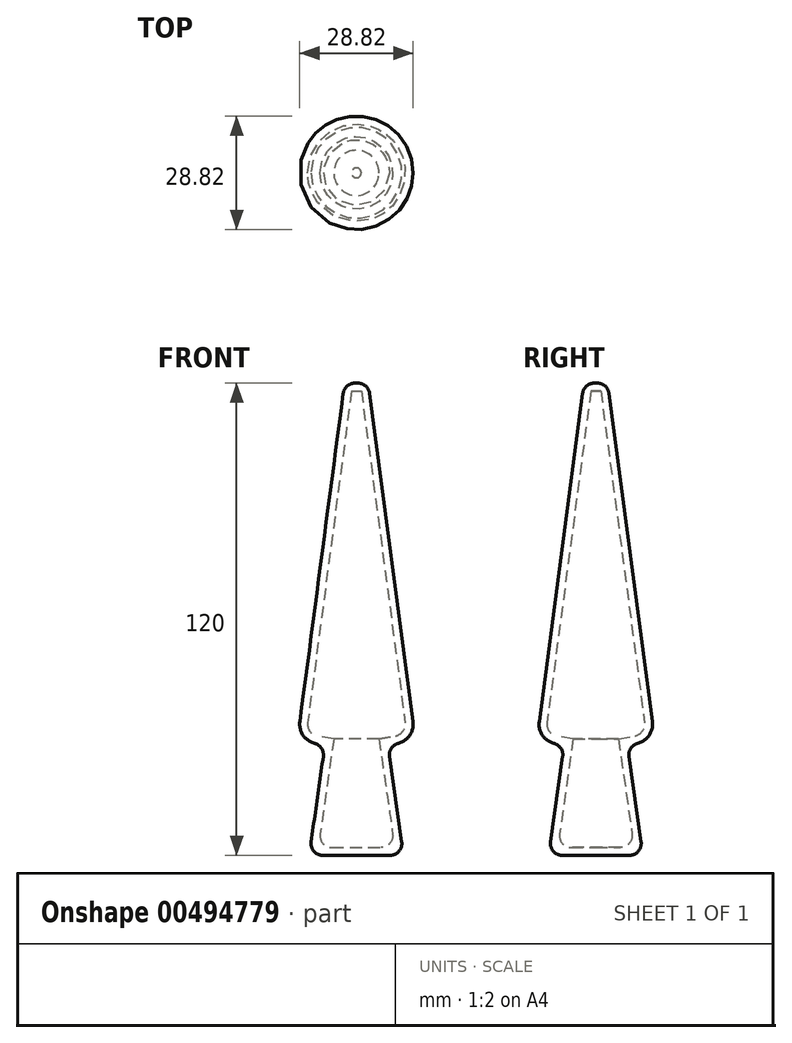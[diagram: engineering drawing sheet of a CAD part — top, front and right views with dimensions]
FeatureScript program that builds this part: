
annotation { "Feature Type Name" : "Feature", "Feature Type Description" : "" }
export const myFeature = defineFeature(function(context is Context, id is Id, definition is map)
    precondition{}
    {
        {
            var Q0;
            Q0=qCreatedBy(makeId("Front.planeOp"),FACE);
            var sketch = newSketch(context, id + "F0", { "sketchPlane" : qUnion([Q0])});
            skLineSegment(sketch, "E0", {"start": v(8, 8) * mm, "end": v(15, 9.22) * mm});
            skLineSegment(sketch, "E1", {"start": v(15, 9.22) * mm, "end": v(3, 100) * mm});
            skLineSegment(sketch, "E2", {"start": v(0, 100) * mm, "end": v(0, -20) * mm});
            skLineSegment(sketch, "E3", {"start": v(0, -27) * mm, "end": v(0, -53.61) * mm});
            skLineSegment(sketch, "E4", {"start": v(0, 100) * mm, "end": v(3, 100) * mm});
            skLineSegment(sketch, "E5", {"start": v(0, 103.57) * mm, "end": v(0, 117.09) * mm});
            skLineSegment(sketch, "E6", {"start": v(0, -20) * mm, "end": v(12, -20) * mm});
            skLineSegment(sketch, "E7", {"start": v(8, 8) * mm, "end": v(12, -20) * mm});
            skSolve(sketch);
        }
        {
            var Q0;
            Q0=makeQuery(id+"F0.imprint","IMPRINT",FACE,{"disambiguationData":[TD([[makeQuery(id+"F0.imprint","IMPRINT",EDGE,{"derivedFrom":sQuery(id+"F0.wireOp",EDGE,"E0")}),1.0]])]});
            var Q1;
            Q1=sQuery(id+"F0.wireOp",EDGE,"E5");
            revolve(context, id + "F1", {"entities" : qUnion([Q0]), "axis" : qUnion([Q1]), "revolveType" : RevolveType.ONE_DIRECTION, "angle" : 180 * degree});
        }
        {
            var Q0;
            Q0=makeQuery(id+"F1.opRevolve","CAP_FACE",FACE,{"disambiguationData":[OSD([sQuery(id+"F0.wireOp",EDGE,"E0"),sQuery(id+"F0.wireOp",EDGE,"E1"),sQuery(id+"F0.wireOp",EDGE,"E2"),sQuery(id+"F0.wireOp",EDGE,"E4"),sQuery(id+"F0.wireOp",EDGE,"E6"),sQuery(id+"F0.wireOp",EDGE,"E7")])],"isStart":false});
            shell(context, id + "F2", {"entities" : qUnion([Q0]), "thickness" : 2 * mm});
        }
        {
            var Q0;
            Q0=makeQuery(id+"F1.opRevolve","SWEPT_BODY",BODY,{"disambiguationData":[OSD([sQuery(id+"F0.wireOp",EDGE,"E0"),sQuery(id+"F0.wireOp",EDGE,"E1"),sQuery(id+"F0.wireOp",EDGE,"E2"),sQuery(id+"F0.wireOp",EDGE,"E4"),sQuery(id+"F0.wireOp",EDGE,"E6"),sQuery(id+"F0.wireOp",EDGE,"E7")])]});
            var Q1;
            Q1=qCreatedBy(makeId("Front.planeOp"),FACE);
            mirror(context, id + "F3", {"operationType" : NewBodyOperationType.ADD, "entities" : qUnion([Q0]), "mirrorPlane" : qUnion([Q1])});
        }
        {
            var Q0;
            {var subQ0=makeQuery(id+"F1.opRevolve","SWEPT_EDGE",EDGE,{"disambiguationData":[OSD([sQuery(id+"F0.wireOp",EDGE,"E0"),sQuery(id+"F0.wireOp",EDGE,"E1")])]});Q0=makeQuery(id+"F3.boolean.opBoolean","MERGE",EDGE,{"derivedFrom":[subQ0,makeQuery(id+"F3.opPattern","COPY",EDGE,{"derivedFrom":subQ0,"instanceName":"1"})]});}
            fillet(context, id + "F4", {"entities" : qUnion([Q0]), "radius" : 5 * mm, "tangentPropagation" : true, "allowEdgeOverflow" : false});
        }
        {
            var Q0;
            {var subQ0=makeQuery(id+"F1.opRevolve","SWEPT_EDGE",EDGE,{"disambiguationData":[OSD([sQuery(id+"F0.wireOp",EDGE,"E6"),sQuery(id+"F0.wireOp",EDGE,"E7")])]});Q0=makeQuery(id+"F3.boolean.opBoolean","MERGE",EDGE,{"derivedFrom":[subQ0,makeQuery(id+"F3.opPattern","COPY",EDGE,{"derivedFrom":subQ0,"instanceName":"1"})]});}
            var Q1;
            {var subQ0=makeQuery(id+"F1.opRevolve","SWEPT_EDGE",EDGE,{"disambiguationData":[OSD([sQuery(id+"F0.wireOp",EDGE,"E1"),sQuery(id+"F0.wireOp",EDGE,"E4")])]});Q1=makeQuery(id+"F3.boolean.opBoolean","MERGE",EDGE,{"derivedFrom":[subQ0,makeQuery(id+"F3.opPattern","COPY",EDGE,{"derivedFrom":subQ0,"instanceName":"1"})]});}
            var Q2;
            {var subQ0=makeQuery(id+"F1.opRevolve","SWEPT_EDGE",EDGE,{"disambiguationData":[OSD([sQuery(id+"F0.wireOp",EDGE,"E0"),sQuery(id+"F0.wireOp",EDGE,"E7")])]});Q2=makeQuery(id+"F3.boolean.opBoolean","MERGE",EDGE,{"derivedFrom":[subQ0,makeQuery(id+"F3.opPattern","COPY",EDGE,{"derivedFrom":subQ0,"instanceName":"1"})]});}
            fillet(context, id + "F5", {"entities" : qUnion([Q0, Q1, Q2]), "radius" : 3 * mm, "tangentPropagation" : true, "allowEdgeOverflow" : false});
        }
        {
            var Q0;
            {var subQ0=makeQuery(id+"F2.opShell","OFFSET_EDGE",EDGE,{"disambiguationData":[OSD([sQuery(id+"F0.wireOp",EDGE,"E0"),sQuery(id+"F0.wireOp",EDGE,"E1")])]});Q0=makeQuery(id+"F3.boolean.opBoolean","MERGE",EDGE,{"derivedFrom":[subQ0,makeQuery(id+"F3.opPattern","COPY",EDGE,{"derivedFrom":subQ0,"instanceName":"1"})]});}
            fillet(context, id + "F6", {"entities" : qUnion([Q0]), "radius" : 3 * mm, "tangentPropagation" : true, "allowEdgeOverflow" : false});
        }
        {
            var Q0;
            {var subQ0=makeQuery(id+"F2.opShell","OFFSET_EDGE",EDGE,{"disambiguationData":[OSD([sQuery(id+"F0.wireOp",EDGE,"E6"),sQuery(id+"F0.wireOp",EDGE,"E7")])]});Q0=makeQuery(id+"F3.boolean.opBoolean","MERGE",EDGE,{"derivedFrom":[subQ0,makeQuery(id+"F3.opPattern","COPY",EDGE,{"derivedFrom":subQ0,"instanceName":"1"})]});}
            fillet(context, id + "F7", {"entities" : qUnion([Q0]), "radius" : 3 * mm, "tangentPropagation" : true, "allowEdgeOverflow" : false});
        }
    });
